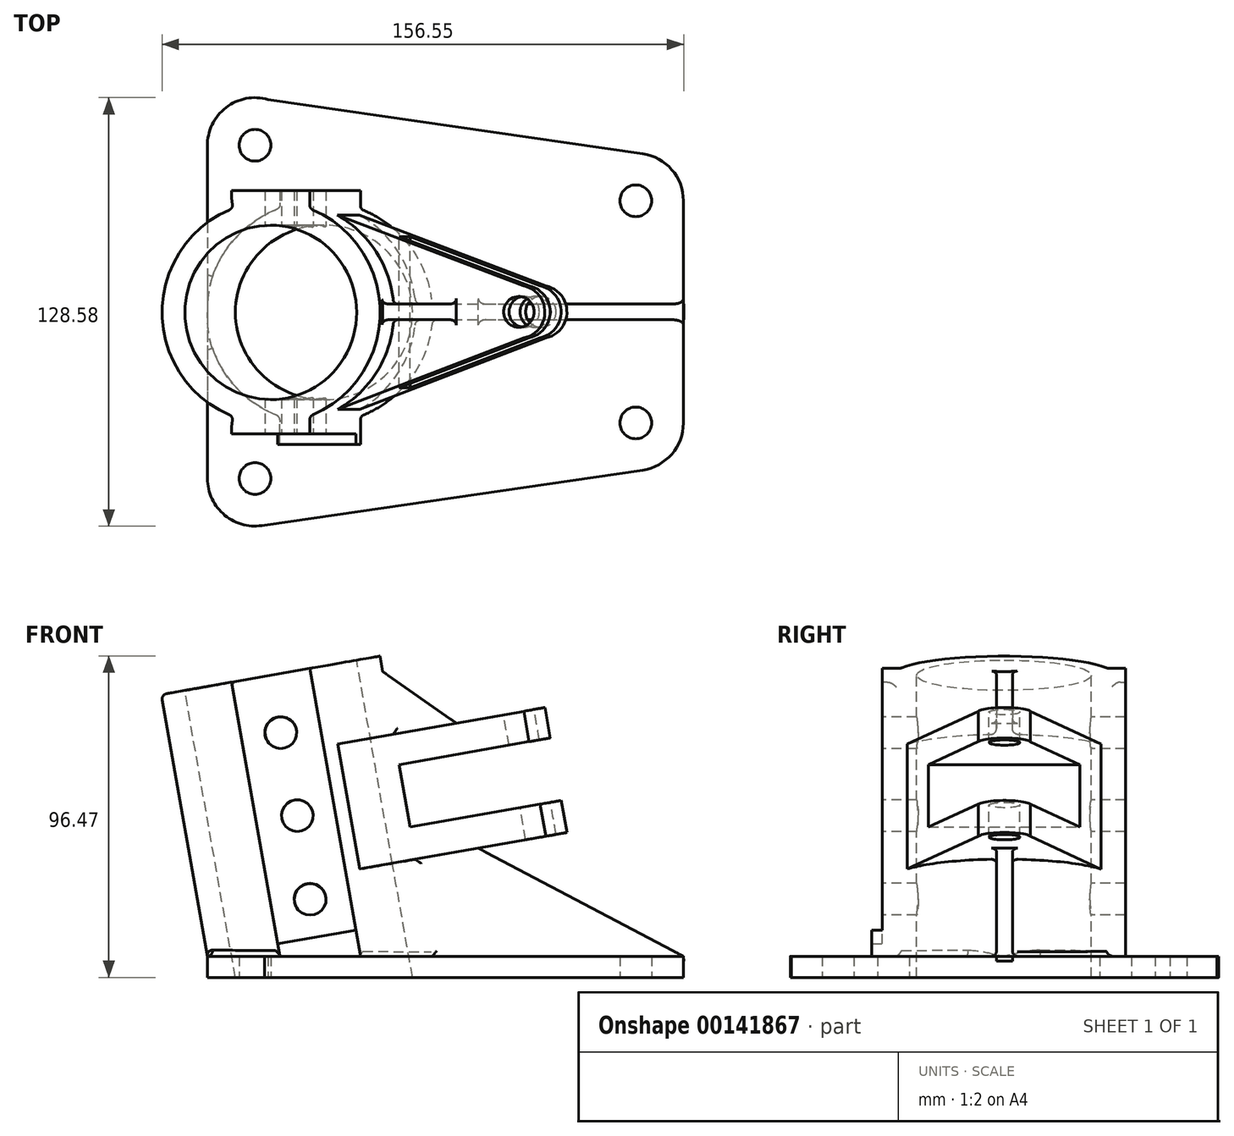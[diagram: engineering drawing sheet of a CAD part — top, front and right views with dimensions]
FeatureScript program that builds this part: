
annotation { "Feature Type Name" : "Feature", "Feature Type Description" : "" }
export const myFeature = defineFeature(function(context is Context, id is Id, definition is map)
    precondition{}
    {
        {
            var Q0;
            Q0=qCreatedBy(makeId("Top.planeOp"),FACE);
            var sketch = newSketch(context, id + "F0", { "sketchPlane" : qUnion([Q0])});
            skPoint(sketch, "E0.middle", {"position": v(0, 0) * mm});
            skPoint(sketch, "E1.endSnap0", {"position": v(-57.15, 0) * mm});
            skCircle(sketch, "E2", {"center": v(57.15, 33.34) * mm, "radius": 4.76 * mm});
            skCircle(sketch, "E3", {"center": v(57.15, -33.34) * mm, "radius": 4.76 * mm});
            skCircle(sketch, "E4", {"center": v(-57.15, -50) * mm, "radius": 4.76 * mm});
            skCircle(sketch, "E5", {"center": v(-57.15, 50) * mm, "radius": 4.76 * mm});
            skArc(sketch, "E6", {"start": v(71.44, 33.34) * mm, "mid": v(67.95, 42.69) * mm, "end": v(59.2, 47.48) * mm});
            skArc(sketch, "E7", {"start": v(-53.24, 63.75) * mm, "mid": v(-65.88, 61.32) * mm, "end": v(-71.43, 49.71) * mm});
            skArc(sketch, "E8.MirrorC", {"start": v(71.44, -33.34) * mm, "mid": v(67.96, -42.68) * mm, "end": v(59.2, -47.48) * mm});
            skArc(sketch, "E9.MirrorC", {"start": v(-54.3, -64) * mm, "mid": v(-66.19, -61.07) * mm, "end": v(-71.44, -50) * mm});
            skLineSegment(sketch, "E10", {"start": v(-57, 64.3) * mm, "end": v(59.2, 47.48) * mm});
            skLineSegment(sketch, "E11", {"start": v(-71.43, 49.71) * mm, "end": v(-71.44, -50) * mm});
            skLineSegment(sketch, "E12", {"start": v(-54.3, -64) * mm, "end": v(59.2, -47.48) * mm});
            skLineSegment(sketch, "E13", {"start": v(71.44, -33.34) * mm, "end": v(71.44, 33.34) * mm});
            skSolve(sketch);
        }
        {
            var Q0;
            Q0 = qSketchRegion(id + "F0", true);
            extrude(context, id + "F1", {"entities" : qUnion([Q0]), "depth" : 6.35 * mm});
        }
        {
            var Q0;
            Q0=qCreatedBy(makeId("Top.planeOp"),FACE);
            var Q1;
            Q1=makeQuery(id+"F1.opExtrude","CAP_EDGE",EDGE,{"disambiguationData":[OSD([sQuery(id+"F0.wireOp",EDGE,"E11")])],"isStart":false});
            cPlane(context, id + "F2", {"entities" : qUnion([Q0, Q1]), "cplaneType" : CPlaneType.LINE_ANGLE, "offset" : 25.4 * mm, "angle" : 10 * degree, "width" : 152.4 * mm, "height" : 152.4 * mm});
        }
        {
            var Q0;
            Q0=qCreatedBy(id+"F2.planeOp",FACE);
            var sketch = newSketch(context, id + "F3", { "sketchPlane" : qUnion([Q0])});
            skLineSegment(sketch, "E14.0", {"start": v(-69.25, -49.71) * mm, "end": v(-69.25, 50) * mm});
            skLineSegment(sketch, "E15", {"start": v(-69.25, 0.15) * mm, "end": v(-2.57, 0.15) * mm});
            skCircle(sketch, "E16", {"center": v(-35.91, 0.15) * mm, "radius": 33.34 * mm});
            skSolve(sketch);
        }
        {
            var Q0;
            Q0=qCreatedBy(makeId("Front.planeOp"),FACE);
            var sketch = newSketch(context, id + "F4", { "sketchPlane" : qUnion([Q0])});
            skFitSpline(sketch, "E17.0.0", {"points": [v(-86.32, 90.77) * mm, v(-86.32, 90.77) * mm, v(-85.9, 90.85) * mm, v(-84.03, 91.18) * mm, v(-80.98, 91.71) * mm, v(-76.87, 92.44) * mm, v(-71.87, 93.32) * mm, v(-64.25, 94.66) * mm, v(-53.5, 96.56) * mm, v(-42.76, 98.45) * mm, v(-35.14, 99.8) * mm, v(-30.13, 100.68) * mm, v(-26.02, 101.4) * mm, v(-22.96, 101.94) * mm, v(-21.08, 102.28) * mm, v(-20.45, 102.39) * mm, v(-21.08, 102.28) * mm, v(-22.96, 101.94) * mm, v(-26.02, 101.4) * mm, v(-30.13, 100.68) * mm, v(-35.14, 99.8) * mm, v(-42.76, 98.45) * mm, v(-53.5, 96.56) * mm, v(-64.25, 94.66) * mm, v(-71.87, 93.32) * mm, v(-76.87, 92.44) * mm, v(-80.98, 91.71) * mm, v(-84.03, 91.18) * mm, v(-85.9, 90.85) * mm, v(-86.32, 90.77) * mm, v(-86.32, 90.77) * mm, v(-86.32, 90.77) * mm]});
            skLineSegment(sketch, "E18", {"start": v(-53.5, 96.56) * mm, "end": v(-36.46, 0) * mm});
            skSolve(sketch);
        }
        {
            var Q0;
            Q0=qCreatedBy(id+"F2.planeOp",FACE);
            var Q1;
            Q1=sQuery(id+"F4.wireOp",VERTEX,"E18.end");
            cPlane(context, id + "F5", {"entities" : qUnion([Q0, Q1]), "cplaneType" : CPlaneType.PLANE_POINT, "offset" : 25.4 * mm, "width" : 152.4 * mm, "height" : 152.4 * mm});
        }
        {
            var Q0;
            Q0=qCreatedBy(id+"F5.planeOp",FACE);
            var sketch = newSketch(context, id + "F6", { "sketchPlane" : qUnion([Q0])});
            skCircle(sketch, "E19.0", {"center": v(-35.91, 0.15) * mm, "radius": 33.34 * mm});
            skSolve(sketch);
        }
        {
            var Q0;
            Q0=makeQuery(id+"F6.imprint","IMPRINT",FACE,{"disambiguationData":[TD([[makeQuery(id+"F6.imprint","IMPRINT",EDGE,{"derivedFrom":sQuery(id+"F6.wireOp",EDGE,"E19.0")}),1.0]])]});
            extrude(context, id + "F7", {"entities" : qUnion([Q0]), "operationType" : NewBodyOperationType.ADD, "oppositeDirection" : true, "depth" : 92.07 * mm});
        }
        {
            var Q0;
            Q0=makeQuery(id+"F7.opExtrude","CAP_FACE",FACE,{"disambiguationData":[OSD([sQuery(id+"F6.wireOp",EDGE,"E19.0")])],"isStart":true});
            var Q1;
            Q1=makeQuery(id+"F1.opExtrude","CAP_FACE",FACE,{"disambiguationData":[OSD([sQuery(id+"F0.wireOp",EDGE,"E2"),sQuery(id+"F0.wireOp",EDGE,"E3"),sQuery(id+"F0.wireOp",EDGE,"E4"),sQuery(id+"F0.wireOp",EDGE,"E5"),sQuery(id+"F0.wireOp",EDGE,"E6"),sQuery(id+"F0.wireOp",EDGE,"E7"),sQuery(id+"F0.wireOp",EDGE,"E8.MirrorC"),sQuery(id+"F0.wireOp",EDGE,"E9.MirrorC"),sQuery(id+"F0.wireOp",EDGE,"E10"),sQuery(id+"F0.wireOp",EDGE,"E11"),sQuery(id+"F0.wireOp",EDGE,"E12"),sQuery(id+"F0.wireOp",EDGE,"E13")])],"isStart":true});
            extrude(context, id + "F8", {"entities" : qUnion([Q0]), "operationType" : NewBodyOperationType.REMOVE, "endBound" : BoundingType.UP_TO_SURFACE, "oppositeDirection" : true, "endBoundEntityFace" : qUnion([Q1]), "depth" : 25.4 * mm});
        }
        {
            var Q0;
            Q0=makeQuery(id+"F7.opExtrude","CAP_FACE",FACE,{"disambiguationData":[OSD([sQuery(id+"F6.wireOp",EDGE,"E19.0")])],"isStart":false});
            var sketch = newSketch(context, id + "F9", { "sketchPlane" : qUnion([Q0])});
            skCircle(sketch, "E20", {"center": v(-35.91, -0.15) * mm, "radius": 26.2 * mm});
            skSolve(sketch);
        }
        {
            var Q0;
            Q0 = qSketchRegion(id + "F9", true);
            extrude(context, id + "F10", {"entities" : qUnion([Q0]), "operationType" : NewBodyOperationType.REMOVE, "endBound" : BoundingType.THROUGH_ALL, "oppositeDirection" : true, "depth" : 25.4 * mm});
        }
        {
            var Q0;
            Q0=makeQuery(id+"F7.opExtrude","CAP_FACE",FACE,{"disambiguationData":[OSD([sQuery(id+"F6.wireOp",EDGE,"E19.0")])],"isStart":false});
            var sketch = newSketch(context, id + "F11", { "sketchPlane" : qUnion([Q0])});
            skLineSegment(sketch, "E21.0", {"start": v(-24, 30.02) * mm, "end": v(-24, 36.37) * mm});
            skLineSegment(sketch, "E22.0", {"start": v(-47.82, 30.02) * mm, "end": v(-47.82, 36.37) * mm});
            skLineSegment(sketch, "E23.0", {"start": v(-47.82, 30.02) * mm, "end": v(-24, 30.02) * mm});
            skLineSegment(sketch, "E24.0", {"start": v(-47.82, 36.37) * mm, "end": v(-24, 36.37) * mm});
            skPoint(sketch, "E25.orphan", {"position": v(-35.91, -0.15) * mm});
            skLineSegment(sketch, "E26.MirrorCS", {"start": v(-24, -30.3) * mm, "end": v(-24, -36.66) * mm});
            skLineSegment(sketch, "E27.MirrorCS", {"start": v(-47.82, -36.66) * mm, "end": v(-24, -36.66) * mm});
            skLineSegment(sketch, "E28.MirrorCS", {"start": v(-47.82, -30.3) * mm, "end": v(-47.82, -36.66) * mm});
            skLineSegment(sketch, "E29.MirrorCS", {"start": v(-47.82, -30.3) * mm, "end": v(-24, -30.3) * mm});
            skSolve(sketch);
        }
        {
            var Q0;
            Q0 = qSketchRegion(id + "F11", true);
            var Q1;
            Q1=makeQuery(id+"F1.opExtrude","CAP_FACE",FACE,{"disambiguationData":[OSD([sQuery(id+"F0.wireOp",EDGE,"E2"),sQuery(id+"F0.wireOp",EDGE,"E3"),sQuery(id+"F0.wireOp",EDGE,"E4"),sQuery(id+"F0.wireOp",EDGE,"E5"),sQuery(id+"F0.wireOp",EDGE,"E6"),sQuery(id+"F0.wireOp",EDGE,"E7"),sQuery(id+"F0.wireOp",EDGE,"E8.MirrorC"),sQuery(id+"F0.wireOp",EDGE,"E9.MirrorC"),sQuery(id+"F0.wireOp",EDGE,"E10"),sQuery(id+"F0.wireOp",EDGE,"E11"),sQuery(id+"F0.wireOp",EDGE,"E12"),sQuery(id+"F0.wireOp",EDGE,"E13")])],"isStart":false});
            extrude(context, id + "F12", {"entities" : qUnion([Q0]), "operationType" : NewBodyOperationType.ADD, "endBound" : BoundingType.UP_TO_SURFACE, "oppositeDirection" : true, "endBoundEntityFace" : qUnion([Q1]), "depth" : 25.4 * mm});
        }
        {
            var Q0;
            Q0=makeQuery(id+"F12.opExtrude","SWEPT_FACE",FACE,{"disambiguationData":[OSD([sQuery(id+"F11.wireOp",EDGE,"E27.MirrorCS")])]});
            var sketch = newSketch(context, id + "F13", { "sketchPlane" : qUnion([Q0])});
            skLineSegment(sketch, "E30", {"start": v(-52.45, 90.68) * mm, "end": v(-36.46, 0) * mm});
            skLineSegment(sketch, "E31.0", {"start": v(-61.15, 71.41) * mm, "end": v(-37.7, 75.55) * mm});
            skLineSegment(sketch, "E32.0", {"start": v(-56.74, 46.4) * mm, "end": v(-33.28, 50.53) * mm});
            skLineSegment(sketch, "E33.0", {"start": v(-52.32, 21.38) * mm, "end": v(-28.87, 25.52) * mm});
            skLineSegment(sketch, "E34.0", {"start": v(-50.67, 12) * mm, "end": v(-27.22, 16.14) * mm});
            skCircle(sketch, "E35", {"center": v(-49.42, 73.48) * mm, "radius": 4.76 * mm});
            skCircle(sketch, "E36", {"center": v(-44.46, 48.56) * mm, "radius": 4.76 * mm});
            skPoint(sketch, "E36.centerSnap0", {"position": v(-44.46, 45.34) * mm});
            skCircle(sketch, "E37", {"center": v(-40.6, 23.45) * mm, "radius": 4.76 * mm});
            skSolve(sketch);
        }
        {
            var Q0;
            Q0 = qSketchRegion(id + "F13", true);
            extrude(context, id + "F14", {"entities" : qUnion([Q0]), "operationType" : NewBodyOperationType.REMOVE, "endBound" : BoundingType.THROUGH_ALL, "oppositeDirection" : true, "depth" : 25.4 * mm});
        }
        {
            var Q0;
            Q0=makeQuery(id+"F12.boolean.opBoolean","MERGE",FACE,{"derivedFrom":[makeQuery(id+"F7.opExtrude","CAP_FACE",FACE,{"disambiguationData":[OSD([sQuery(id+"F6.wireOp",EDGE,"E19.0")])],"isStart":false}),makeQuery(id+"F12.opExtrude","CAP_FACE",FACE,{"disambiguationData":[OSD([sQuery(id+"F11.wireOp",EDGE,"E21.0"),sQuery(id+"F11.wireOp",EDGE,"E22.0"),sQuery(id+"F11.wireOp",EDGE,"E23.0"),sQuery(id+"F11.wireOp",EDGE,"E24.0")])],"isStart":true}),makeQuery(id+"F12.opExtrude","CAP_FACE",FACE,{"disambiguationData":[OSD([sQuery(id+"F11.wireOp",EDGE,"E26.MirrorCS"),sQuery(id+"F11.wireOp",EDGE,"E27.MirrorCS"),sQuery(id+"F11.wireOp",EDGE,"E28.MirrorCS"),sQuery(id+"F11.wireOp",EDGE,"E29.MirrorCS")])],"isStart":true})]});
            cPlane(context, id + "F15", {"entities" : qUnion([Q0]), "cplaneType" : CPlaneType.OFFSET, "offset" : 23.8 * mm, "oppositeDirection" : true, "width" : 152.4 * mm, "height" : 152.4 * mm});
        }
        {
            var Q0;
            Q0=qCreatedBy(id+"F15.planeOp",FACE);
            var sketch = newSketch(context, id + "F16", { "sketchPlane" : qUnion([Q0])});
            skPoint(sketch, "E38.0", {"position": v(-35.91, -0.15) * mm});
            skCircle(sketch, "E39", {"center": v(35.53, 0) * mm, "radius": 4.64 * mm});
            skArc(sketch, "E40", {"start": v(37.02, -7.8) * mm, "mid": v(43.46, 0.02) * mm, "end": v(36.98, 7.8) * mm});
            skArc(sketch, "E41.0", {"start": v(-19.75, 29) * mm, "mid": v(-2.57, -0.08) * mm, "end": v(-19.63, -29.24) * mm});
            skLineSegment(sketch, "E42", {"start": v(-19.75, 29) * mm, "end": v(36.98, 7.8) * mm});
            skLineSegment(sketch, "E43.MirrorCS", {"start": v(-19.63, -29.24) * mm, "end": v(37.02, -7.8) * mm});
            skPoint(sketch, "E44.orphan", {"position": v(-24, 31) * mm});
            skPoint(sketch, "E45.orphan", {"position": v(-24, -31.29) * mm});
            skSolve(sketch);
        }
        {
            var Q0;
            Q0 = qSketchRegion(id + "F16", true);
            extrude(context, id + "F17", {"entities" : qUnion([Q0]), "operationType" : NewBodyOperationType.ADD, "oppositeDirection" : true, "depth" : 38.1 * mm});
        }
        {
            var Q0;
            Q0=qCreatedBy(makeId("Front.planeOp"),FACE);
            var sketch = newSketch(context, id + "F18", { "sketchPlane" : qUnion([Q0])});
            skLineSegment(sketch, "E46", {"start": v(-21.37, 93.58) * mm, "end": v(4.6, 75.4) * mm});
            skLineSegment(sketch, "E47", {"start": v(7.7, 39.94) * mm, "end": v(71.44, 6.35) * mm});
            skLineSegment(sketch, "E48", {"start": v(-21.37, 93.59) * mm, "end": v(-17.04, 70.24) * mm});
            skLineSegment(sketch, "E49", {"start": v(-17.04, 70.24) * mm, "end": v(4.6, 75.4) * mm});
            skLineSegment(sketch, "E50", {"start": v(7.7, 39.94) * mm, "end": v(-12.23, 35.49) * mm});
            skLineSegment(sketch, "E51", {"start": v(-12.23, 35.49) * mm, "end": v(-5.4, 4.9) * mm});
            skLineSegment(sketch, "E52", {"start": v(-5.4, 4.9) * mm, "end": v(71.52, 4.9) * mm});
            skLineSegment(sketch, "E53", {"start": v(71.52, 4.9) * mm, "end": v(71.44, 6.35) * mm});
            skSolve(sketch);
        }
        {
            var Q0;
            Q0 = qSketchRegion(id + "F18", true);
            extrude(context, id + "F19", {"entities" : qUnion([Q0]), "operationType" : NewBodyOperationType.ADD, "endBound" : BoundingType.SYMMETRIC, "depth" : 4.76 * mm});
        }
        {
            var Q0;
            Q0=qCreatedBy(makeId("Front.planeOp"),FACE);
            var sketch = newSketch(context, id + "F20", { "sketchPlane" : qUnion([Q0])});
            skLineSegment(sketch, "E54", {"start": v(-13.88, 63.88) * mm, "end": v(-10.57, 45.12) * mm});
            skLineSegment(sketch, "E55.0", {"start": v(-13.88, 63.88) * mm, "end": v(41, 73.56) * mm});
            skLineSegment(sketch, "E56.0", {"start": v(-10.57, 45.12) * mm, "end": v(41.66, 54.33) * mm});
            skPoint(sketch, "E57.orphan", {"position": v(-48.32, 67.23) * mm});
            skPoint(sketch, "E58.0.end.orphan", {"position": v(22.03, 79.63) * mm});
            skLineSegment(sketch, "E59", {"start": v(41, 73.56) * mm, "end": v(41.66, 54.33) * mm});
            skSolve(sketch);
        }
        {
            var Q0;
            Q0 = qSketchRegion(id + "F20", true);
            extrude(context, id + "F21", {"entities" : qUnion([Q0]), "operationType" : NewBodyOperationType.REMOVE, "endBound" : BoundingType.SYMMETRIC, "depth" : 76.2 * mm});
        }
        {
            var Q0;
            Q0=qCreatedBy(id+"F2.planeOp",FACE);
            var sketch = newSketch(context, id + "F22", { "sketchPlane" : qUnion([Q0])});
            skLineSegment(sketch, "E60.0", {"start": v(-47.82, 33.48) * mm, "end": v(-24, 33.48) * mm});
            skLineSegment(sketch, "E61.0", {"start": v(-47.82, 39.83) * mm, "end": v(-24, 39.83) * mm});
            skLineSegment(sketch, "E62", {"start": v(-24, 39.83) * mm, "end": v(-24, 33.48) * mm});
            skLineSegment(sketch, "E63", {"start": v(-47.82, 39.83) * mm, "end": v(-47.82, 33.48) * mm});
            skPoint(sketch, "E64.0.end.orphan", {"position": v(-24, 36.66) * mm});
            skPoint(sketch, "E64.0.start.orphan", {"position": v(-47.82, 36.66) * mm});
            skSolve(sketch);
        }
        {
            var Q0;
            Q0 = qSketchRegion(id + "F22", true);
            var Q1;
            {var subQ0=sQuery(id+"F0.wireOp",EDGE,"E12");var subQ1=sQuery(id+"F0.wireOp",EDGE,"E11");var subQ2=sQuery(id+"F0.wireOp",EDGE,"E9.MirrorC");var subQ3=sQuery(id+"F0.wireOp",EDGE,"E13");var subQ4=sQuery(id+"F0.wireOp",EDGE,"E8.MirrorC");var subQ5=sQuery(id+"F0.wireOp",EDGE,"E4");var subQ6=sQuery(id+"F0.wireOp",EDGE,"E3");var subQ7=makeQuery(id+"F1.opExtrude","CAP_FACE",FACE,{"disambiguationData":[OSD([sQuery(id+"F0.wireOp",EDGE,"E2"),subQ6,subQ5,sQuery(id+"F0.wireOp",EDGE,"E5"),sQuery(id+"F0.wireOp",EDGE,"E6"),sQuery(id+"F0.wireOp",EDGE,"E7"),subQ4,subQ2,sQuery(id+"F0.wireOp",EDGE,"E10"),subQ1,subQ0,subQ3])],"isStart":false});Q1=makeQuery(id+"F19.boolean.opBoolean","SPLIT",FACE,{"disambiguationData":[TD([makeQuery(id+"F1.opExtrude","SWEPT_FACE",FACE,{"disambiguationData":[OSD([subQ6])]})])],"derivedFrom":subQ7});}
            extrude(context, id + "F23", {"entities" : qUnion([Q0]), "operationType" : NewBodyOperationType.ADD, "endBound" : BoundingType.UP_TO_SURFACE, "endBoundEntityFace" : qUnion([Q1]), "depth" : 25.4 * mm});
        }
        {
            var Q0;
            {var subQ0=sQuery(id+"F0.wireOp",EDGE,"E11");var subQ1=sQuery(id+"F6.wireOp",EDGE,"E19.0");Q0=makeQuery(id+"F12.boolean.opBoolean","INTERSECT",EDGE,{"derivedFrom":[makeQuery(id+"F7.boolean.opBoolean","SPLIT",FACE,{"disambiguationData":[TD([makeQuery(id+"F1.opExtrude","SWEPT_FACE",FACE,{"disambiguationData":[OSD([subQ0])]})])],"derivedFrom":makeQuery(id+"F7.opExtrude","SWEPT_FACE",FACE,{"disambiguationData":[OSD([subQ1])]})}),makeQuery(id+"F12.opExtrude","SWEPT_FACE",FACE,{"disambiguationData":[OSD([sQuery(id+"F11.wireOp",EDGE,"E26.MirrorCS")])]})]});}
            var Q1;
            {var subQ0=sQuery(id+"F0.wireOp",EDGE,"E11");var subQ1=sQuery(id+"F6.wireOp",EDGE,"E19.0");Q1=makeQuery(id+"F12.boolean.opBoolean","INTERSECT",EDGE,{"derivedFrom":[makeQuery(id+"F7.boolean.opBoolean","SPLIT",FACE,{"disambiguationData":[TD([makeQuery(id+"F1.opExtrude","SWEPT_FACE",FACE,{"disambiguationData":[OSD([subQ0])]})])],"derivedFrom":makeQuery(id+"F7.opExtrude","SWEPT_FACE",FACE,{"disambiguationData":[OSD([subQ1])]})}),makeQuery(id+"F12.opExtrude","SWEPT_FACE",FACE,{"disambiguationData":[OSD([sQuery(id+"F11.wireOp",EDGE,"E28.MirrorCS")])]})]});}
            var Q2;
            {var subQ0=sQuery(id+"F0.wireOp",EDGE,"E11");var subQ1=sQuery(id+"F6.wireOp",EDGE,"E19.0");Q2=makeQuery(id+"F12.boolean.opBoolean","INTERSECT",EDGE,{"derivedFrom":[makeQuery(id+"F7.boolean.opBoolean","SPLIT",FACE,{"disambiguationData":[TD([makeQuery(id+"F1.opExtrude","SWEPT_FACE",FACE,{"disambiguationData":[OSD([subQ0])]})])],"derivedFrom":makeQuery(id+"F7.opExtrude","SWEPT_FACE",FACE,{"disambiguationData":[OSD([subQ1])]})}),makeQuery(id+"F12.opExtrude","SWEPT_FACE",FACE,{"disambiguationData":[OSD([sQuery(id+"F11.wireOp",EDGE,"E22.0")])]})]});}
            var Q3;
            {var subQ0=sQuery(id+"F0.wireOp",EDGE,"E11");var subQ1=sQuery(id+"F6.wireOp",EDGE,"E19.0");Q3=makeQuery(id+"F12.boolean.opBoolean","INTERSECT",EDGE,{"derivedFrom":[makeQuery(id+"F7.boolean.opBoolean","SPLIT",FACE,{"disambiguationData":[TD([makeQuery(id+"F1.opExtrude","SWEPT_FACE",FACE,{"disambiguationData":[OSD([subQ0])]})])],"derivedFrom":makeQuery(id+"F7.opExtrude","SWEPT_FACE",FACE,{"disambiguationData":[OSD([subQ1])]})}),makeQuery(id+"F12.opExtrude","SWEPT_FACE",FACE,{"disambiguationData":[OSD([sQuery(id+"F11.wireOp",EDGE,"E21.0")])]})]});}
            var Q4;
            {var subQ0=makeQuery(id+"F1.opExtrude","CAP_FACE",FACE,{"disambiguationData":[OSD([sQuery(id+"F0.wireOp",EDGE,"E2"),sQuery(id+"F0.wireOp",EDGE,"E3"),sQuery(id+"F0.wireOp",EDGE,"E4"),sQuery(id+"F0.wireOp",EDGE,"E5"),sQuery(id+"F0.wireOp",EDGE,"E6"),sQuery(id+"F0.wireOp",EDGE,"E7"),sQuery(id+"F0.wireOp",EDGE,"E8.MirrorC"),sQuery(id+"F0.wireOp",EDGE,"E9.MirrorC"),sQuery(id+"F0.wireOp",EDGE,"E10"),sQuery(id+"F0.wireOp",EDGE,"E11"),sQuery(id+"F0.wireOp",EDGE,"E12"),sQuery(id+"F0.wireOp",EDGE,"E13")])],"isStart":false});var subQ1=makeQuery(id+"F7.opExtrude","SWEPT_FACE",FACE,{"disambiguationData":[OSD([sQuery(id+"F6.wireOp",EDGE,"E19.0")])]});var subQ2=makeQuery(id+"F12.opExtrude","SWEPT_FACE",FACE,{"disambiguationData":[OSD([sQuery(id+"F11.wireOp",EDGE,"E21.0")])]});Q4=makeQuery(id+"F19.boolean.opBoolean","SPLIT",EDGE,{"disambiguationData":[TD([subQ2])],"derivedFrom":makeQuery(id+"F12.boolean.opBoolean","SPLIT",EDGE,{"disambiguationData":[TD([subQ2])],"derivedFrom":makeQuery(id+"F7.boolean.opBoolean","INTERSECT",EDGE,{"derivedFrom":[subQ0,subQ1]})})});}
            var Q5;
            {var subQ0=sQuery(id+"F11.wireOp",EDGE,"E21.0");var subQ1=sQuery(id+"F6.wireOp",EDGE,"E19.0");var subQ3=sQuery(id+"F0.wireOp",EDGE,"E11");Q5=makeQuery(id+"F19.boolean.opBoolean","INTERSECT",EDGE,{"derivedFrom":[makeQuery(id+"F12.boolean.opBoolean","SPLIT",FACE,{"disambiguationData":[TD([makeQuery(id+"F12.opExtrude","SWEPT_FACE",FACE,{"disambiguationData":[OSD([subQ0])]})])],"derivedFrom":makeQuery(id+"F7.boolean.opBoolean","SPLIT",FACE,{"disambiguationData":[TD([makeQuery(id+"F1.opExtrude","SWEPT_FACE",FACE,{"disambiguationData":[OSD([subQ3])]})])],"derivedFrom":makeQuery(id+"F7.opExtrude","SWEPT_FACE",FACE,{"disambiguationData":[OSD([subQ1])]})})}),makeQuery(id+"F19.opExtrude","CAP_FACE",FACE,{"disambiguationData":[OSD([sQuery(id+"F18.wireOp",EDGE,"E46"),sQuery(id+"F18.wireOp",EDGE,"E48"),sQuery(id+"F18.wireOp",EDGE,"E49")])],"isStart":false})]});}
            var Q6;
            Q6=makeQuery(id+"F19.boolean.opBoolean","INTERSECT",EDGE,{"derivedFrom":[makeQuery(id+"F17.opExtrude","CAP_FACE",FACE,{"disambiguationData":[OSD([sQuery(id+"F16.wireOp",EDGE,"E39"),sQuery(id+"F16.wireOp",EDGE,"E40"),sQuery(id+"F16.wireOp",EDGE,"E41.0"),sQuery(id+"F16.wireOp",EDGE,"E42"),sQuery(id+"F16.wireOp",EDGE,"E43.MirrorCS")])],"isStart":true}),makeQuery(id+"F19.opExtrude","CAP_FACE",FACE,{"disambiguationData":[OSD([sQuery(id+"F18.wireOp",EDGE,"E46"),sQuery(id+"F18.wireOp",EDGE,"E48"),sQuery(id+"F18.wireOp",EDGE,"E49")])],"isStart":false})]});
            var Q7;
            Q7=makeQuery(id+"F19.boolean.opBoolean","INTERSECT",EDGE,{"derivedFrom":[makeQuery(id+"F1.opExtrude","CAP_FACE",FACE,{"disambiguationData":[OSD([sQuery(id+"F0.wireOp",EDGE,"E2"),sQuery(id+"F0.wireOp",EDGE,"E3"),sQuery(id+"F0.wireOp",EDGE,"E4"),sQuery(id+"F0.wireOp",EDGE,"E5"),sQuery(id+"F0.wireOp",EDGE,"E6"),sQuery(id+"F0.wireOp",EDGE,"E7"),sQuery(id+"F0.wireOp",EDGE,"E8.MirrorC"),sQuery(id+"F0.wireOp",EDGE,"E9.MirrorC"),sQuery(id+"F0.wireOp",EDGE,"E10"),sQuery(id+"F0.wireOp",EDGE,"E11"),sQuery(id+"F0.wireOp",EDGE,"E12"),sQuery(id+"F0.wireOp",EDGE,"E13")])],"isStart":false}),makeQuery(id+"F19.opExtrude","CAP_FACE",FACE,{"disambiguationData":[OSD([sQuery(id+"F18.wireOp",EDGE,"E47"),sQuery(id+"F18.wireOp",EDGE,"E50"),sQuery(id+"F18.wireOp",EDGE,"E51"),sQuery(id+"F18.wireOp",EDGE,"E52"),sQuery(id+"F18.wireOp",EDGE,"E53")])],"isStart":false})]});
            var Q8;
            {var subQ0=sQuery(id+"F11.wireOp",EDGE,"E21.0");var subQ1=sQuery(id+"F6.wireOp",EDGE,"E19.0");var subQ3=sQuery(id+"F0.wireOp",EDGE,"E11");Q8=makeQuery(id+"F19.boolean.opBoolean","INTERSECT",EDGE,{"derivedFrom":[makeQuery(id+"F12.boolean.opBoolean","SPLIT",FACE,{"disambiguationData":[TD([makeQuery(id+"F12.opExtrude","SWEPT_FACE",FACE,{"disambiguationData":[OSD([subQ0])]})])],"derivedFrom":makeQuery(id+"F7.boolean.opBoolean","SPLIT",FACE,{"disambiguationData":[TD([makeQuery(id+"F1.opExtrude","SWEPT_FACE",FACE,{"disambiguationData":[OSD([subQ3])]})])],"derivedFrom":makeQuery(id+"F7.opExtrude","SWEPT_FACE",FACE,{"disambiguationData":[OSD([subQ1])]})})}),makeQuery(id+"F19.opExtrude","CAP_FACE",FACE,{"disambiguationData":[OSD([sQuery(id+"F18.wireOp",EDGE,"E47"),sQuery(id+"F18.wireOp",EDGE,"E50"),sQuery(id+"F18.wireOp",EDGE,"E51"),sQuery(id+"F18.wireOp",EDGE,"E52"),sQuery(id+"F18.wireOp",EDGE,"E53")])],"isStart":false})]});}
            var Q9;
            Q9=makeQuery(id+"F17.opExtrude","SWEPT_EDGE",EDGE,{"disambiguationData":[OSD([sQuery(id+"F16.wireOp",EDGE,"E41.0"),sQuery(id+"F16.wireOp",EDGE,"E43.MirrorCS")])]});
            var Q10;
            {var subQ0=sQuery(id+"F16.wireOp",EDGE,"E43.MirrorCS");var subQ1=sQuery(id+"F16.wireOp",EDGE,"E41.0");Q10=makeQuery(id+"F19.boolean.opBoolean","SPLIT",EDGE,{"disambiguationData":[TD([makeQuery(id+"F17.opExtrude","SWEPT_FACE",FACE,{"disambiguationData":[OSD([subQ0])]})])],"derivedFrom":makeQuery(id+"F17.opExtrude","CAP_EDGE",EDGE,{"disambiguationData":[OSD([subQ1])],"isStart":true})});}
            var Q11;
            Q11=makeQuery(id+"F19.boolean.opBoolean","INTERSECT",EDGE,{"derivedFrom":[makeQuery(id+"F17.opExtrude","CAP_FACE",FACE,{"disambiguationData":[OSD([sQuery(id+"F16.wireOp",EDGE,"E39"),sQuery(id+"F16.wireOp",EDGE,"E40"),sQuery(id+"F16.wireOp",EDGE,"E41.0"),sQuery(id+"F16.wireOp",EDGE,"E42"),sQuery(id+"F16.wireOp",EDGE,"E43.MirrorCS")])],"isStart":false}),makeQuery(id+"F19.opExtrude","CAP_FACE",FACE,{"disambiguationData":[OSD([sQuery(id+"F18.wireOp",EDGE,"E47"),sQuery(id+"F18.wireOp",EDGE,"E50"),sQuery(id+"F18.wireOp",EDGE,"E51"),sQuery(id+"F18.wireOp",EDGE,"E52"),sQuery(id+"F18.wireOp",EDGE,"E53")])],"isStart":false})]});
            var Q12;
            {var subQ0=sQuery(id+"F16.wireOp",EDGE,"E43.MirrorCS");var subQ1=sQuery(id+"F16.wireOp",EDGE,"E41.0");Q12=makeQuery(id+"F19.boolean.opBoolean","SPLIT",EDGE,{"disambiguationData":[TD([makeQuery(id+"F17.opExtrude","SWEPT_FACE",FACE,{"disambiguationData":[OSD([subQ0])]})])],"derivedFrom":makeQuery(id+"F17.opExtrude","CAP_EDGE",EDGE,{"disambiguationData":[OSD([subQ1])],"isStart":false})});}
            var Q13;
            {var subQ0=sQuery(id+"F11.wireOp",EDGE,"E21.0");var subQ1=sQuery(id+"F6.wireOp",EDGE,"E19.0");var subQ3=sQuery(id+"F0.wireOp",EDGE,"E11");Q13=makeQuery(id+"F19.boolean.opBoolean","INTERSECT",EDGE,{"derivedFrom":[makeQuery(id+"F12.boolean.opBoolean","SPLIT",FACE,{"disambiguationData":[TD([makeQuery(id+"F12.opExtrude","SWEPT_FACE",FACE,{"disambiguationData":[OSD([subQ0])]})])],"derivedFrom":makeQuery(id+"F7.boolean.opBoolean","SPLIT",FACE,{"disambiguationData":[TD([makeQuery(id+"F1.opExtrude","SWEPT_FACE",FACE,{"disambiguationData":[OSD([subQ3])]})])],"derivedFrom":makeQuery(id+"F7.opExtrude","SWEPT_FACE",FACE,{"disambiguationData":[OSD([subQ1])]})})}),makeQuery(id+"F19.opExtrude","CAP_FACE",FACE,{"disambiguationData":[OSD([sQuery(id+"F18.wireOp",EDGE,"E47"),sQuery(id+"F18.wireOp",EDGE,"E50"),sQuery(id+"F18.wireOp",EDGE,"E51"),sQuery(id+"F18.wireOp",EDGE,"E52"),sQuery(id+"F18.wireOp",EDGE,"E53")])],"isStart":true})]});}
            var Q14;
            Q14=makeQuery(id+"F19.boolean.opBoolean","INTERSECT",EDGE,{"derivedFrom":[makeQuery(id+"F17.opExtrude","CAP_FACE",FACE,{"disambiguationData":[OSD([sQuery(id+"F16.wireOp",EDGE,"E39"),sQuery(id+"F16.wireOp",EDGE,"E40"),sQuery(id+"F16.wireOp",EDGE,"E41.0"),sQuery(id+"F16.wireOp",EDGE,"E42"),sQuery(id+"F16.wireOp",EDGE,"E43.MirrorCS")])],"isStart":false}),makeQuery(id+"F19.opExtrude","CAP_FACE",FACE,{"disambiguationData":[OSD([sQuery(id+"F18.wireOp",EDGE,"E47"),sQuery(id+"F18.wireOp",EDGE,"E50"),sQuery(id+"F18.wireOp",EDGE,"E51"),sQuery(id+"F18.wireOp",EDGE,"E52"),sQuery(id+"F18.wireOp",EDGE,"E53")])],"isStart":true})]});
            var Q15;
            Q15=makeQuery(id+"F19.boolean.opBoolean","INTERSECT",EDGE,{"derivedFrom":[makeQuery(id+"F1.opExtrude","CAP_FACE",FACE,{"disambiguationData":[OSD([sQuery(id+"F0.wireOp",EDGE,"E2"),sQuery(id+"F0.wireOp",EDGE,"E3"),sQuery(id+"F0.wireOp",EDGE,"E4"),sQuery(id+"F0.wireOp",EDGE,"E5"),sQuery(id+"F0.wireOp",EDGE,"E6"),sQuery(id+"F0.wireOp",EDGE,"E7"),sQuery(id+"F0.wireOp",EDGE,"E8.MirrorC"),sQuery(id+"F0.wireOp",EDGE,"E9.MirrorC"),sQuery(id+"F0.wireOp",EDGE,"E10"),sQuery(id+"F0.wireOp",EDGE,"E11"),sQuery(id+"F0.wireOp",EDGE,"E12"),sQuery(id+"F0.wireOp",EDGE,"E13")])],"isStart":false}),makeQuery(id+"F19.opExtrude","CAP_FACE",FACE,{"disambiguationData":[OSD([sQuery(id+"F18.wireOp",EDGE,"E47"),sQuery(id+"F18.wireOp",EDGE,"E50"),sQuery(id+"F18.wireOp",EDGE,"E51"),sQuery(id+"F18.wireOp",EDGE,"E52"),sQuery(id+"F18.wireOp",EDGE,"E53")])],"isStart":true})]});
            var Q16;
            {var subQ1=sQuery(id+"F6.wireOp",EDGE,"E19.0");var subQ3=sQuery(id+"F0.wireOp",EDGE,"E11");var subQ4=makeQuery(id+"F1.opExtrude","SWEPT_FACE",FACE,{"disambiguationData":[OSD([subQ3])]});Q16=makeQuery(id+"F12.boolean.opBoolean","SPLIT",FACE,{"disambiguationData":[TD([subQ4])],"derivedFrom":makeQuery(id+"F7.boolean.opBoolean","SPLIT",FACE,{"disambiguationData":[TD([subQ4])],"derivedFrom":makeQuery(id+"F7.opExtrude","SWEPT_FACE",FACE,{"disambiguationData":[OSD([subQ1])]})})});}
            var Q17;
            {var subQ0=sQuery(id+"F11.wireOp",EDGE,"E21.0");var subQ1=sQuery(id+"F6.wireOp",EDGE,"E19.0");var subQ3=sQuery(id+"F0.wireOp",EDGE,"E11");Q17=makeQuery(id+"F19.boolean.opBoolean","INTERSECT",EDGE,{"derivedFrom":[makeQuery(id+"F12.boolean.opBoolean","SPLIT",FACE,{"disambiguationData":[TD([makeQuery(id+"F12.opExtrude","SWEPT_FACE",FACE,{"disambiguationData":[OSD([subQ0])]})])],"derivedFrom":makeQuery(id+"F7.boolean.opBoolean","SPLIT",FACE,{"disambiguationData":[TD([makeQuery(id+"F1.opExtrude","SWEPT_FACE",FACE,{"disambiguationData":[OSD([subQ3])]})])],"derivedFrom":makeQuery(id+"F7.opExtrude","SWEPT_FACE",FACE,{"disambiguationData":[OSD([subQ1])]})})}),makeQuery(id+"F19.opExtrude","CAP_FACE",FACE,{"disambiguationData":[OSD([sQuery(id+"F18.wireOp",EDGE,"E46"),sQuery(id+"F18.wireOp",EDGE,"E48"),sQuery(id+"F18.wireOp",EDGE,"E49")])],"isStart":true})]});}
            var Q18;
            Q18=makeQuery(id+"F19.boolean.opBoolean","INTERSECT",EDGE,{"derivedFrom":[makeQuery(id+"F17.opExtrude","CAP_FACE",FACE,{"disambiguationData":[OSD([sQuery(id+"F16.wireOp",EDGE,"E39"),sQuery(id+"F16.wireOp",EDGE,"E40"),sQuery(id+"F16.wireOp",EDGE,"E41.0"),sQuery(id+"F16.wireOp",EDGE,"E42"),sQuery(id+"F16.wireOp",EDGE,"E43.MirrorCS")])],"isStart":true}),makeQuery(id+"F19.opExtrude","CAP_FACE",FACE,{"disambiguationData":[OSD([sQuery(id+"F18.wireOp",EDGE,"E46"),sQuery(id+"F18.wireOp",EDGE,"E48"),sQuery(id+"F18.wireOp",EDGE,"E49")])],"isStart":true})]});
            var Q19;
            {var subQ0=sQuery(id+"F16.wireOp",EDGE,"E42");var subQ1=sQuery(id+"F16.wireOp",EDGE,"E41.0");Q19=makeQuery(id+"F19.boolean.opBoolean","SPLIT",EDGE,{"disambiguationData":[TD([makeQuery(id+"F17.opExtrude","SWEPT_FACE",FACE,{"disambiguationData":[OSD([subQ0])]})])],"derivedFrom":makeQuery(id+"F17.opExtrude","CAP_EDGE",EDGE,{"disambiguationData":[OSD([subQ1])],"isStart":true})});}
            var Q20;
            {var subQ0=sQuery(id+"F16.wireOp",EDGE,"E42");var subQ1=sQuery(id+"F16.wireOp",EDGE,"E41.0");Q20=makeQuery(id+"F19.boolean.opBoolean","SPLIT",EDGE,{"disambiguationData":[TD([makeQuery(id+"F17.opExtrude","SWEPT_FACE",FACE,{"disambiguationData":[OSD([subQ0])]})])],"derivedFrom":makeQuery(id+"F17.opExtrude","CAP_EDGE",EDGE,{"disambiguationData":[OSD([subQ1])],"isStart":false})});}
            fillet(context, id + "F24", {"entities" : qUnion([Q0, Q1, Q2, Q3, Q4, Q5, Q6, Q7, Q8, Q9, Q10, Q11, Q12, Q13, Q14, Q15, Q16, Q17, Q18, Q19, Q20]), "radius" : 1.59 * mm, "tangentPropagation" : true, "allowEdgeOverflow" : false});
        }
    });
